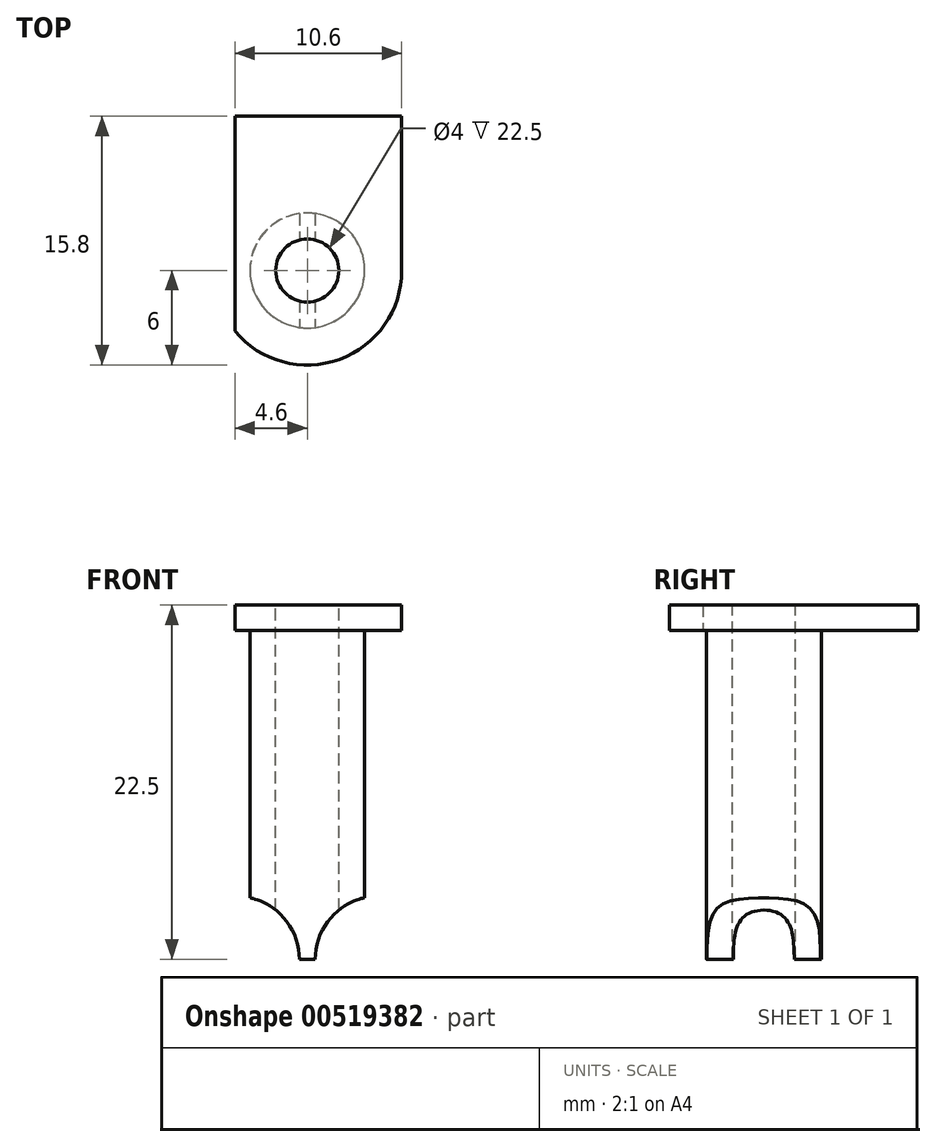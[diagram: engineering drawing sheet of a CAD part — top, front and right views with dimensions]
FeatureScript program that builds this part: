
annotation { "Feature Type Name" : "Feature", "Feature Type Description" : "" }
export const myFeature = defineFeature(function(context is Context, id is Id, definition is map)
    precondition{}
    {
        {
            var Q0;
            Q0=qCreatedBy(makeId("Top.planeOp"),FACE);
            var sketch = newSketch(context, id + "F0", { "sketchPlane" : qUnion([Q0])});
            skArc(sketch, "E0", {"start": v(-4.6, -3.85) * mm, "mid": v(2.05, -5.64) * mm, "end": v(6, 0) * mm});
            skLineSegment(sketch, "E1", {"start": v(6, 0) * mm, "end": v(6, 9.8) * mm});
            skLineSegment(sketch, "E2", {"start": v(6, 9.8) * mm, "end": v(-4.6, 9.8) * mm});
            skLineSegment(sketch, "E3", {"start": v(-4.6, 9.8) * mm, "end": v(-4.6, -3.85) * mm});
            skSolve(sketch);
        }
        {
            var Q0;
            Q0 = qSketchRegion(id + "F0", true);
            extrude(context, id + "F1", {"entities" : qUnion([Q0]), "depth" : 1.6 * mm, "offsetDistance" : 25 * mm});
        }
        {
            var Q0;
            Q0=makeQuery(id+"F1.opExtrude","CAP_FACE",FACE,{"disambiguationData":[OSD([sQuery(id+"F0.wireOp",EDGE,"E0"),sQuery(id+"F0.wireOp",EDGE,"E1"),sQuery(id+"F0.wireOp",EDGE,"E2"),sQuery(id+"F0.wireOp",EDGE,"E3")])],"isStart":true});
            var sketch = newSketch(context, id + "F2", { "sketchPlane" : qUnion([Q0])});
            skCircle(sketch, "E4", {"center": v(0, 0) * mm, "radius": 3.65 * mm});
            skSolve(sketch);
        }
        {
            var Q0;
            Q0 = qSketchRegion(id + "F2", true);
            extrude(context, id + "F3", {"entities" : qUnion([Q0]), "operationType" : NewBodyOperationType.ADD, "depth" : (22.5 - 1.6) * mm, "offsetDistance" : 25 * mm});
        }
        {
            var Q0;
            Q0=qCreatedBy(makeId("Front.planeOp"),FACE);
            var sketch = newSketch(context, id + "F4", { "sketchPlane" : qUnion([Q0])});
            skCircle(sketch, "E5", {"center": v(4.5, -20.9) * mm, "radius": 4 * mm});
            skCircle(sketch, "E6", {"center": v(-4.5, -20.9) * mm, "radius": 4 * mm});
            skSolve(sketch);
        }
        {
            var Q0;
            Q0 = qSketchRegion(id + "F4", true);
            extrude(context, id + "F5", {"entities" : qUnion([Q0]), "operationType" : NewBodyOperationType.REMOVE, "oppositeDirection" : true, "depth" : 25 * mm, "offsetDistance" : 25 * mm, "hasSecondDirection" : true, "secondDirectionOppositeDirection" : false, "secondDirectionDepth" : 25 * mm});
        }
        {
            var Q0;
            Q0=makeQuery(id+"F1.opExtrude","CAP_FACE",FACE,{"disambiguationData":[OSD([sQuery(id+"F0.wireOp",EDGE,"E0"),sQuery(id+"F0.wireOp",EDGE,"E1"),sQuery(id+"F0.wireOp",EDGE,"E2"),sQuery(id+"F0.wireOp",EDGE,"E3")])],"isStart":false});
            var sketch = newSketch(context, id + "F6", { "sketchPlane" : qUnion([Q0])});
            skCircle(sketch, "E7", {"center": v(0, 0) * mm, "radius": 2 * mm});
            skSolve(sketch);
        }
        {
            var Q0;
            Q0 = qSketchRegion(id + "F6", true);
            extrude(context, id + "F7", {"entities" : qUnion([Q0]), "operationType" : NewBodyOperationType.REMOVE, "endBound" : BoundingType.THROUGH_ALL, "oppositeDirection" : true, "depth" : 25 * mm, "offsetDistance" : 25 * mm});
        }
    });
